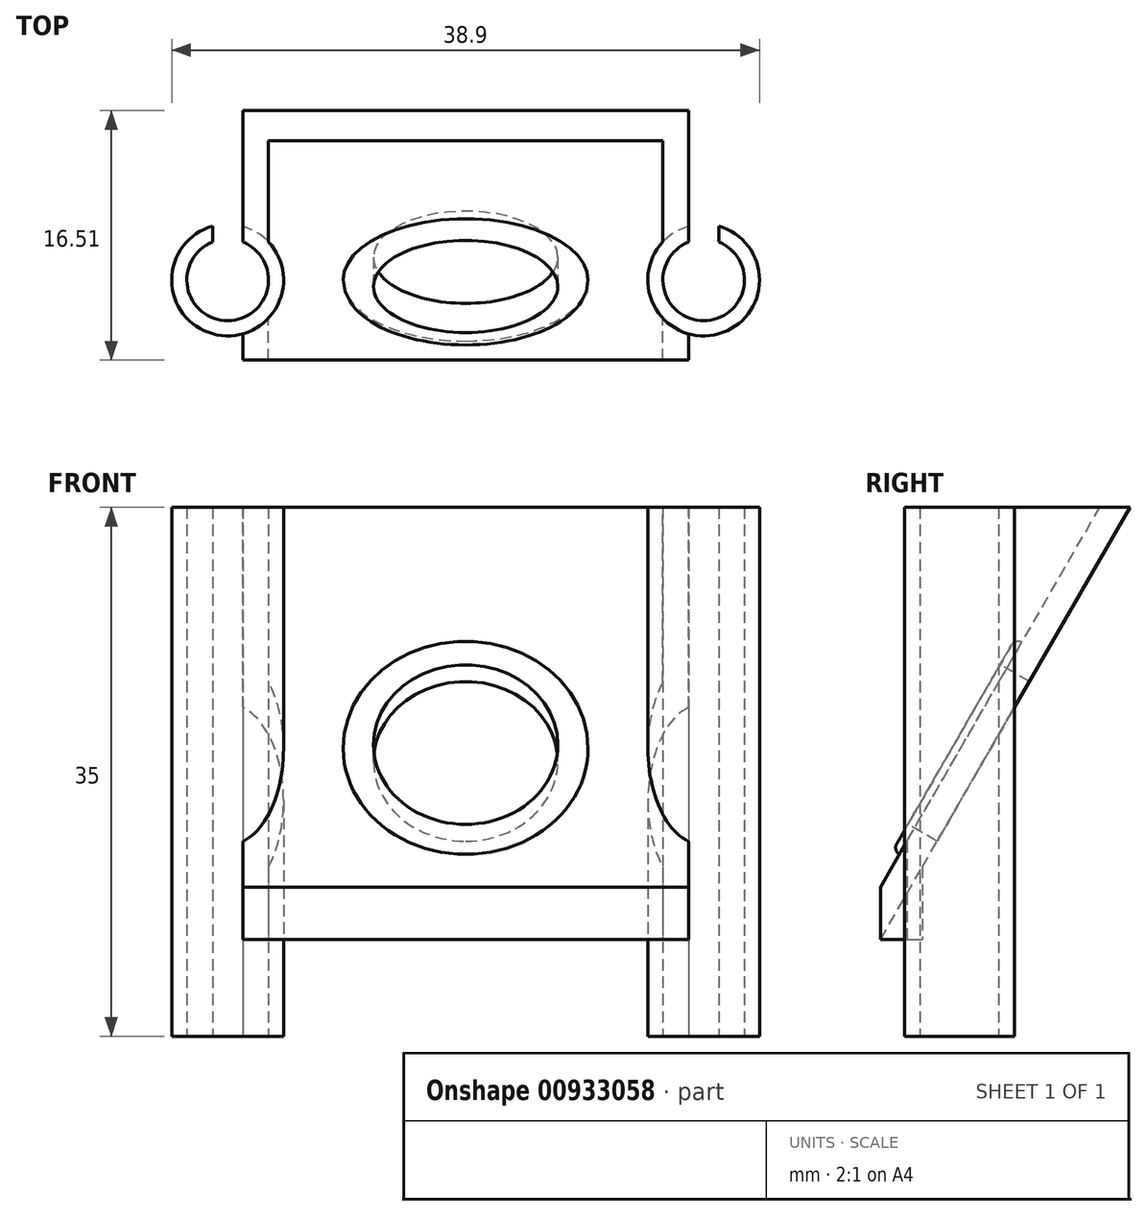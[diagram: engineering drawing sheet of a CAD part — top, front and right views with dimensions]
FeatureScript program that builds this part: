
annotation { "Feature Type Name" : "Feature", "Feature Type Description" : "" }
export const myFeature = defineFeature(function(context is Context, id is Id, definition is map)
    precondition{}
    {
        {
            var Q0;
            Q0=qCreatedBy(makeId("Top.planeOp"),FACE);
            var sketch = newSketch(context, id + "F0", { "sketchPlane" : qUnion([Q0])});
            skLineSegment(sketch, "E0", {"start": v(0, 0) * mm, "end": v(-15.75, 0) * mm, "construction": true});
            skCircle(sketch, "E1", {"center": v(-15.75, 0) * mm, "radius": 2.7 * mm});
            skCircle(sketch, "E2.0", {"center": v(-15.75, 0) * mm, "radius": 3.7 * mm});
            skSolve(sketch);
        }
        {
            var Q0;
            Q0=qSketchRegion(id+"F0",true);
            extrude(context, id + "F1", {"entities" : qUnion([Q0]), "offsetDistance" : 25 * mm, "depth" : 35 * mm});
        }
        {
            var Q0;
            Q0=qCreatedBy(makeId("Top.planeOp"),FACE);
            var sketch = newSketch(context, id + "F2", { "sketchPlane" : qUnion([Q0])});
            skCircle(sketch, "E3.0", {"center": v(-15.75, 0) * mm, "radius": 2.7 * mm, "construction": true});
            skLineSegment(sketch, "E4", {"start": v(-15.75, 0) * mm, "end": v(-15.75, 2.7) * mm, "construction": true});
            skLineSegment(sketch, "E5.bottom", {"start": v(-14.75, 5.76) * mm, "end": v(-16.75, 5.76) * mm});
            skLineSegment(sketch, "E5.top", {"start": v(-14.75, -0.36) * mm, "end": v(-16.75, -0.36) * mm});
            skLineSegment(sketch, "E5.left", {"start": v(-14.75, 5.76) * mm, "end": v(-14.75, -0.36) * mm});
            skLineSegment(sketch, "E5.right", {"start": v(-16.75, 5.76) * mm, "end": v(-16.75, -0.36) * mm});
            skPoint(sketch, "E5.middle", {"position": v(-15.75, 2.7) * mm});
            skSolve(sketch);
        }
        {
            var Q0;
            Q0=qSketchRegion(id+"F2",true);
            extrude(context, id + "F3", {"entities" : qUnion([Q0]), "operationType" : NewBodyOperationType.REMOVE, "endBound" : BoundingType.THROUGH_ALL, "depth" : 25 * mm});
        }
        {
            var Q0;
            Q0=qCreatedBy(makeId("Top.planeOp"),FACE);
            cPlane(context, id + "F4", {"entities" : qUnion([Q0]), "cplaneType" : CPlaneType.OFFSET, "offset" : 35 * mm, "width" : 150 * mm, "height" : 150 * mm});
        }
        {
            var Q0;
            Q0=makeQuery(id+"F1.opExtrude","SWEPT_BODY",BODY,{"disambiguationData":[OSD([sQuery(id+"F0.wireOp",EDGE,"E1"),sQuery(id+"F0.wireOp",EDGE,"E2.0")])]});
            var Q1;
            Q1=qCreatedBy(makeId("Right.planeOp"),FACE);
            mirror(context, id + "F5", {"entities" : qUnion([Q0]), "mirrorPlane" : qUnion([Q1])});
        }
        {
            var Q0;
            Q0=qCreatedBy(makeId("Top.planeOp"),FACE);
            var sketch = newSketch(context, id + "F6", { "sketchPlane" : qUnion([Q0])});
            skPoint(sketch, "E6.middle", {"position": v(0, 0) * mm});
            skLineSegment(sketch, "E7.bottom", {"start": v(-13.05, -11) * mm, "end": v(13.05, -11) * mm});
            skLineSegment(sketch, "E7.top", {"start": v(-13.05, -9) * mm, "end": v(13.05, -9) * mm});
            skLineSegment(sketch, "E7.left", {"start": v(-13.05, -11) * mm, "end": v(-13.05, -9) * mm});
            skLineSegment(sketch, "E7.right", {"start": v(13.05, -11) * mm, "end": v(13.05, -9) * mm});
            skPoint(sketch, "E8", {"position": v(-13.05, 0) * mm});
            skPoint(sketch, "E9", {"position": v(13.05, 0) * mm});
            skSolve(sketch);
        }
        {
            var Q0;
            Q0=qCreatedBy(makeId("Right.planeOp"),FACE);
            var sketch = newSketch(context, id + "F7", { "sketchPlane" : qUnion([Q0])});
            skLineSegment(sketch, "E10", {"start": v(-10, 0) * mm, "end": v(10.2, 35) * mm, "construction": true});
            skLineSegment(sketch, "E11", {"start": v(10.2, 35) * mm, "end": v(10.2, 0) * mm, "construction": true});
            skLineSegment(sketch, "E12", {"start": v(10.2, 0) * mm, "end": v(-10, 0) * mm, "construction": true});
            skSolve(sketch);
        }
        {
            var Q0;
            Q0=qCreatedBy(id+"F4.planeOp",FACE);
            var sketch = newSketch(context, id + "F8", { "sketchPlane" : qUnion([Q0])});
            skLineSegment(sketch, "E13.bottom", {"start": v(13.05, 9.2) * mm, "end": v(-13.05, 9.2) * mm});
            skLineSegment(sketch, "E13.top", {"start": v(13.05, 11.2) * mm, "end": v(-13.05, 11.2) * mm});
            skLineSegment(sketch, "E13.left", {"start": v(13.05, 9.2) * mm, "end": v(13.05, 11.2) * mm});
            skLineSegment(sketch, "E13.right", {"start": v(-13.05, 9.2) * mm, "end": v(-13.05, 11.2) * mm});
            skPoint(sketch, "E13.middle", {"position": v(0, 10.2) * mm});
            skSolve(sketch);
        }
        {
            var Q0;
            Q0=qSketchRegion(id+"F6",true);
            var Q1;
            Q1=qSketchRegion(id+"F8",true);
            loft(context, id + "F9", {"operationType" : NewBodyOperationType.ADD, "sheetProfilesArray" : [{ "sheetProfileEntities" : qUnion([Q0]) }, { "sheetProfileEntities" : qUnion([Q1]) }]});
        }
        {
            var Q0;
            Q0=makeQuery(id+"F9.opLoft","SWEPT_FACE",FACE,{"disambiguationData":[OSD([sQuery(id+"F6.wireOp",EDGE,"E6.bottom"),sQuery(id+"F6.wireOp",EDGE,"E6.top"),sQuery(id+"F6.wireOp",EDGE,"E6.left"),sQuery(id+"F8.wireOp",EDGE,"E13.bottom"),sQuery(id+"F8.wireOp",EDGE,"E13.top"),sQuery(id+"F8.wireOp",EDGE,"E13.left")])]});
            var sketch = newSketch(context, id + "F10", { "sketchPlane" : qUnion([Q0])});
            skLineSegment(sketch, "E14.0", {"start": v(2.53, 19.97) * mm, "end": v(11.2, 35) * mm});
            skLineSegment(sketch, "E15.0", {"start": v(2.5, 0) * mm, "end": v(2.5, 35) * mm});
            skLineSegment(sketch, "E16", {"start": v(2.5, 35) * mm, "end": v(11.2, 35) * mm});
            skLineSegment(sketch, "E17", {"start": v(2.53, 19.97) * mm, "end": v(2.5, 19.93) * mm});
            skSolve(sketch);
        }
        {
            var Q0;
            Q0=qSketchRegion(id+"F10",true);
            var Q1;
            Q1=makeQuery(id+"F5.opPattern","COPY",FACE,{"derivedFrom":makeQuery(id+"F3.boolean.opBoolean","COPY",FACE,{"derivedFrom":makeQuery(id+"F3.opExtrude","SWEPT_FACE",FACE,{"disambiguationData":[OSD([sQuery(id+"F2.wireOp",EDGE,"E5.left")])]})}),"instanceName":"1"});
            extrude(context, id + "F11", {"entities" : qUnion([Q0]), "operationType" : NewBodyOperationType.ADD, "endBound" : BoundingType.UP_TO_SURFACE, "endBoundEntityFace" : qUnion([Q1]), "depth" : 2 * mm});
        }
        {
            var Q0;
            Q0=makeQuery(id+"F9.opLoft","SWEPT_FACE",FACE,{"disambiguationData":[OSD([sQuery(id+"F6.wireOp",EDGE,"E6.bottom"),sQuery(id+"F6.wireOp",EDGE,"E6.top"),sQuery(id+"F6.wireOp",EDGE,"E6.right"),sQuery(id+"F8.wireOp",EDGE,"E13.bottom"),sQuery(id+"F8.wireOp",EDGE,"E13.top"),sQuery(id+"F8.wireOp",EDGE,"E13.right")])]});
            var sketch = newSketch(context, id + "F12", { "sketchPlane" : qUnion([Q0])});
            skLineSegment(sketch, "E18.0", {"start": v(-2.53, 19.97) * mm, "end": v(-11.2, 35) * mm});
            skLineSegment(sketch, "E19.0", {"start": v(-2.5, 0) * mm, "end": v(-2.5, 35) * mm});
            skLineSegment(sketch, "E20", {"start": v(-11.2, 35) * mm, "end": v(-2.5, 35) * mm});
            skLineSegment(sketch, "E21", {"start": v(-2.53, 19.97) * mm, "end": v(-2.5, 19.93) * mm});
            skSolve(sketch);
        }
        {
            var Q0;
            Q0=qSketchRegion(id+"F12",true);
            var Q1;
            Q1=makeQuery(id+"F3.boolean.opBoolean","COPY",FACE,{"derivedFrom":makeQuery(id+"F3.opExtrude","SWEPT_FACE",FACE,{"disambiguationData":[OSD([sQuery(id+"F2.wireOp",EDGE,"E5.left")])]})});
            extrude(context, id + "F13", {"entities" : qUnion([Q0]), "operationType" : NewBodyOperationType.ADD, "endBound" : BoundingType.UP_TO_SURFACE, "endBoundEntityFace" : qUnion([Q1]), "depth" : 25 * mm});
        }
        {
            var Q0;
            Q0=makeQuery(id+"F9.opLoft","SWEPT_FACE",FACE,{"disambiguationData":[OSD([sQuery(id+"F6.wireOp",EDGE,"E6.bottom"),sQuery(id+"F6.wireOp",EDGE,"E6.left"),sQuery(id+"F6.wireOp",EDGE,"E6.right"),sQuery(id+"F8.wireOp",EDGE,"E13.bottom"),sQuery(id+"F8.wireOp",EDGE,"E13.left"),sQuery(id+"F8.wireOp",EDGE,"E13.right")])]});
            var sketch = newSketch(context, id + "F14", { "sketchPlane" : qUnion([Q0])});
            skCircle(sketch, "E22", {"center": v(0, 16.5) * mm, "radius": 6.1 * mm});
            skLineSegment(sketch, "E23", {"start": v(0, -5.5) * mm, "end": v(0, 34.91) * mm, "construction": true});
            skCircle(sketch, "E24", {"center": v(0, 16.5) * mm, "radius": 8.1 * mm});
            skSolve(sketch);
        }
        {
            var Q0;
            Q0=makeQuery(id+"F14.imprint","IMPRINT",FACE,{"disambiguationData":[TD([[makeQuery(id+"F14.imprint","IMPRINT",EDGE,{"derivedFrom":sQuery(id+"F14.wireOp",EDGE,"E22")}),1.0]])]});
            extrude(context, id + "F15", {"entities" : qUnion([Q0]), "operationType" : NewBodyOperationType.REMOVE, "endBound" : BoundingType.THROUGH_ALL, "oppositeDirection" : true, "offsetDistance" : 25 * mm, "depth" : 25 * mm});
        }
        {
            var Q0;
            Q0=makeQuery(id+"F14.imprint","IMPRINT",FACE,{"disambiguationData":[TD([[makeQuery(id+"F14.imprint","IMPRINT",EDGE,{"derivedFrom":sQuery(id+"F14.wireOp",EDGE,"E22")}),-1.0]])]});
            extrude(context, id + "F16", {"entities" : qUnion([Q0]), "operationType" : NewBodyOperationType.ADD, "depth" : 0.5 * mm, "offsetDistance" : 25 * mm});
        }
        {
            var Q0;
            Q0=makeQuery(id+"F16.opExtrude","CAP_EDGE",EDGE,{"disambiguationData":[OSD([sQuery(id+"F14.wireOp",EDGE,"E24")])],"isStart":false});
            fillet(context, id + "F17", {"entities" : qUnion([Q0]), "radius" : 0.5 * mm, "tangentPropagation" : true, "allowEdgeOverflow" : false});
        }
        {
            var Q0;
            {var subQ1=sQuery(id+"F8.wireOp",EDGE,"E13.left");var subQ2=sQuery(id+"F8.wireOp",EDGE,"E13.top");var subQ3=sQuery(id+"F6.wireOp",EDGE,"E7.right");var subQ5=sQuery(id+"F6.wireOp",EDGE,"E7.top");var subQ6=sQuery(id+"F8.wireOp",EDGE,"E13.bottom");var subQ7=sQuery(id+"F6.wireOp",EDGE,"E7.bottom");Q0=makeQuery(id+"F9.boolean.opBoolean","SPLIT",FACE,{"disambiguationData":[TD([makeQuery(id+"F9.opLoft","CAP_FACE",FACE,{"disambiguationData":[OSD([makeQuery(id+"F6.imprint","IMPRINT",FACE,{"disambiguationData":[TD([[makeQuery(id+"F6.imprint","IMPRINT",EDGE,{"derivedFrom":subQ7}),1.0]])]})])],"isStart":true})])],"derivedFrom":makeQuery(id+"F9.opLoft","SWEPT_FACE",FACE,{"disambiguationData":[OSD([subQ7,subQ5,subQ3,subQ6,subQ2,subQ1])]})});}
            var sketch = newSketch(context, id + "F18", { "sketchPlane" : qUnion([Q0])});
            skLineSegment(sketch, "E25.0", {"start": v(-11, 0) * mm, "end": v(-9, 0) * mm});
            skLineSegment(sketch, "E26.0", {"start": v(-11, 0) * mm, "end": v(-2.53, 14.67) * mm});
            skLineSegment(sketch, "E27.0", {"start": v(-9, 0) * mm, "end": v(-2.53, 11.2) * mm});
            skLineSegment(sketch, "E28", {"start": v(-5.3, 9.87) * mm, "end": v(-5.3, 6.4) * mm});
            skLineSegment(sketch, "E29.0", {"start": v(-4.05, 12.04) * mm, "end": v(4.05, 26.07) * mm});
            skSolve(sketch);
        }
        {
            var Q0;
            Q0=qSketchRegion(id+"F18",true);
            extrude(context, id + "F19", {"entities" : qUnion([Q0]), "operationType" : NewBodyOperationType.REMOVE, "endBound" : BoundingType.UP_TO_NEXT, "oppositeDirection" : true, "depth" : 25 * mm, "offsetDistance" : 25 * mm});
        }
        {
            var Q0;
            {var subQ1=sQuery(id+"F8.wireOp",EDGE,"E13.left");var subQ2=sQuery(id+"F8.wireOp",EDGE,"E13.top");var subQ3=sQuery(id+"F6.wireOp",EDGE,"E7.right");var subQ5=sQuery(id+"F6.wireOp",EDGE,"E7.top");var subQ6=sQuery(id+"F8.wireOp",EDGE,"E13.bottom");var subQ7=sQuery(id+"F6.wireOp",EDGE,"E7.bottom");Q0=makeQuery(id+"F9.boolean.opBoolean","SPLIT",FACE,{"disambiguationData":[TD([makeQuery(id+"F9.opLoft","CAP_FACE",FACE,{"disambiguationData":[OSD([makeQuery(id+"F6.imprint","IMPRINT",FACE,{"disambiguationData":[TD([[makeQuery(id+"F6.imprint","IMPRINT",EDGE,{"derivedFrom":subQ7}),1.0]])]})])],"isStart":true})])],"derivedFrom":makeQuery(id+"F9.opLoft","SWEPT_FACE",FACE,{"disambiguationData":[OSD([subQ7,subQ5,subQ3,subQ6,subQ2,subQ1])]})});}
            var sketch = newSketch(context, id + "F20", { "sketchPlane" : qUnion([Q0])});
            skLineSegment(sketch, "E30.0", {"start": v(-5.3, 9.87) * mm, "end": v(-5.3, 6.4) * mm});
            skLineSegment(sketch, "E31.0", {"start": v(-5.3, 9.87) * mm, "end": v(-2.53, 14.67) * mm});
            skLineSegment(sketch, "E32", {"start": v(-5.3, 6.4) * mm, "end": v(-2.53, 6.4) * mm});
            skLineSegment(sketch, "E33", {"start": v(-2.53, 6.4) * mm, "end": v(-2.53, 14.67) * mm});
            skSolve(sketch);
        }
        {
            var Q0;
            Q0 = qSketchRegion(id + "F20", true);
            var Q1;
            Q1=makeQuery(id+"F11.boolean.opBoolean","MERGE",FACE,{"derivedFrom":[makeQuery(id+"F5.opPattern","COPY",FACE,{"derivedFrom":makeQuery(id+"F3.boolean.opBoolean","COPY",FACE,{"derivedFrom":makeQuery(id+"F3.opExtrude","SWEPT_FACE",FACE,{"disambiguationData":[OSD([sQuery(id+"F2.wireOp",EDGE,"E5.left")])]})}),"instanceName":"1"}),makeQuery(id+"F11.opExtrude","CAP_FACE",FACE,{"disambiguationData":[OSD([sQuery(id+"F10.wireOp",EDGE,"E14.0"),sQuery(id+"F10.wireOp",EDGE,"E15.0"),sQuery(id+"F10.wireOp",EDGE,"E16"),sQuery(id+"F10.wireOp",EDGE,"E17")])],"isStart":false})]});
            extrude(context, id + "F21", {"entities" : qUnion([Q0]), "operationType" : NewBodyOperationType.ADD, "endBound" : BoundingType.UP_TO_SURFACE, "depth" : 25 * mm, "endBoundEntityFace" : qUnion([Q1]), "offsetDistance" : 25 * mm});
        }
        {
            var Q0;
            {var subQ0=sQuery(id+"F8.wireOp",EDGE,"E13.right");var subQ2=sQuery(id+"F8.wireOp",EDGE,"E13.bottom");var subQ4=sQuery(id+"F6.wireOp",EDGE,"E7.left");var subQ5=sQuery(id+"F6.wireOp",EDGE,"E7.bottom");var subQ6=sQuery(id+"F8.wireOp",EDGE,"E13.top");var subQ7=sQuery(id+"F6.wireOp",EDGE,"E7.top");Q0=makeQuery(id+"F9.boolean.opBoolean","SPLIT",FACE,{"disambiguationData":[TD([makeQuery(id+"F9.opLoft","CAP_FACE",FACE,{"disambiguationData":[OSD([makeQuery(id+"F6.imprint","IMPRINT",FACE,{"disambiguationData":[TD([[makeQuery(id+"F6.imprint","IMPRINT",EDGE,{"derivedFrom":subQ5}),1.0]])]})])],"isStart":true})])],"derivedFrom":makeQuery(id+"F9.opLoft","SWEPT_FACE",FACE,{"disambiguationData":[OSD([subQ5,subQ7,subQ4,subQ2,subQ6,subQ0])]})});}
            var sketch = newSketch(context, id + "F22", { "sketchPlane" : qUnion([Q0])});
            skLineSegment(sketch, "E34.0", {"start": v(5.3, 9.87) * mm, "end": v(2.53, 14.67) * mm});
            skLineSegment(sketch, "E35.0", {"start": v(5.3, 9.87) * mm, "end": v(5.3, 6.4) * mm});
            skLineSegment(sketch, "E36", {"start": v(2.53, 14.67) * mm, "end": v(2.53, 6.4) * mm});
            skLineSegment(sketch, "E37", {"start": v(2.53, 6.4) * mm, "end": v(5.3, 6.4) * mm});
            skSolve(sketch);
        }
        {
            var Q0;
            Q0 = qSketchRegion(id + "F22", true);
            var Q1;
            Q1=makeQuery(id+"F13.boolean.opBoolean","MERGE",FACE,{"derivedFrom":[makeQuery(id+"F3.boolean.opBoolean","COPY",FACE,{"derivedFrom":makeQuery(id+"F3.opExtrude","SWEPT_FACE",FACE,{"disambiguationData":[OSD([sQuery(id+"F2.wireOp",EDGE,"E5.left")])]})}),makeQuery(id+"F13.opExtrude","CAP_FACE",FACE,{"disambiguationData":[OSD([sQuery(id+"F12.wireOp",EDGE,"E18.0"),sQuery(id+"F12.wireOp",EDGE,"E19.0"),sQuery(id+"F12.wireOp",EDGE,"E20"),sQuery(id+"F12.wireOp",EDGE,"E21")])],"isStart":false})]});
            extrude(context, id + "F23", {"entities" : qUnion([Q0]), "operationType" : NewBodyOperationType.ADD, "endBound" : BoundingType.UP_TO_SURFACE, "depth" : 25 * mm, "endBoundEntityFace" : qUnion([Q1]), "offsetDistance" : 25 * mm});
        }
    });
